# Revit family: Supply_Kit-Faucet-Waterworks-Universal-Angle-Compression
name_source: partatom
category: Plumbing Fixtures
revit_build: Autodesk Revit MEP 2014 (Build: 20140709_2115(x64)
units: mm (PartAtom-declared; Revit-internal decimal feet)

## types (16) — shared parameters
ADA Compliant = Yes
Assembly Code = D2010
CW Connection = Yes
Certification IAPMO = Yes
Certification NSF = Yes
Certification State of MA = Yes
Certification cUPC = Yes
Code Compliance = Code # FDMS32: Certified with IAPMO, NSF, City of LA & IAPMO-CA.
Cold Water Inlet Connection = Inlet - Compression
Cold Water Outlet Connection = Outlet- Compression
Default Elevation = 2' - 10"
Depth = 0' - 3 13/16"
HW Connection = Yes
Hot Limit Safety Stop = No
Hot Water Inlet Connection = Inlet - Compression
Hot Water Outlet Connection = Outlet - Compression
Inlet Connection Diameter = 0' - 0 1/2"
Keynote = 22 40 00
Length = 0' - 11"
Manufacturer = Waterworks
Model = UNMS32
Outlet Connection Diameter = 0' - 0 3/8"
Pressure = 45.00 psi
Product Documentation Link = http://assets.waterworks.com
Product Name = Universal Angle Faucet Supply Kits 1/2” Compression x 3/8” O.D. Compression
Product Page URL = http://www.waterworks.com
URL = http://www.waterworks.com
Vent Connection = No
Version = 2014 - v1.0a
Warranty = http://www.waterworks.com
Waste Connection = No
Water Pressure = Max: 85psi / Min: 20psi / Recommended: 45psi
‌Installation Requirements or Notes = Available option that complies with 0.25% Weighted Average Lead Content (WALC)
zero-valued in all types: CWFU, HWFU, WFU

## per-type parameters (varying)
| type | Constraint | Description | Finish | Model SKU |
| Antique Brass Complies with 0.25% WALC | 1 | Universal Angle Faucet Supply Kits 1/2” Compression x 3/8” O.D. Compression in Antique Brass Complies with 0.25% WALC | Metal - Waterworks - Antique Brass | 26-09876-57740 |
| Antique Copper Complies with 0.25% WALC | 2 | Universal Angle Faucet Supply Kits 1/2” Compression x 3/8” O.D. Compression in Antique Copper Complies with 0.25% WALC | Metal - Waterworks - Antique Copper | 26-73946-90196 |
| Architectural Bronze | 3 | Universal Angle Faucet Supply Kits 1/2” Compression x 3/8” O.D. Compression in Architectural Bronze | Metal - Waterworks - Architectural Bronze | 26-74676-98700 |
| Architectural Bronze Complies with 0.25% WALC | 4 | Universal Angle Faucet Supply Kits 1/2” Compression x 3/8” O.D. Compression in Architectural Bronze Complies with 0.25% WALC | Metal - Waterworks - Architectural Bronze | 26-70415-45280 |
| Burnished Brass Complies with 0.25% WALC | 6 | Universal Angle Faucet Supply Kits 1/2” Compression x 3/8” O.D. Compression in Burnished Brass Complies with 0.25% WALC | Metal - Waterworks - Burnished Brass | 26-48004-36693 |
| Burnished Nickel Complies with 0.25% WALC | 7 | Universal Angle Faucet Supply Kits 1/2” Compression x 3/8” O.D. Compression in Burnished Nickel Complies with 0.25% WALC | Metal - Waterworks - Burnished Nickel | 26-58991-27656 |
| Carbon Complies with 0.25% WALC | 8 | Universal Angle Faucet Supply Kits 1/2” Compression x 3/8” O.D. Compression in Carbon Complies with 0.25% WALC | Metal - Waterworks - Carbon | 26-06550-99717 |
| Chrome Complies with 0.25% WALC | 9 | Universal Angle Faucet Supply Kits 1/2” Compression x 3/8” O.D. Compression in Chrome Complies with 0.25% WALC | Metal - Waterworks - Chrome | 26-24536-85990 |
| Gold Complies with 0.25% WALC | 10 | Universal Angle Faucet Supply Kits 1/2” Compression x 3/8” O.D. Compression in Gold Complies with 0.25% WALC | Metal - Waterworks - Gold | 26-64518-46027 |
| Graphite | 11 | Universal Angle Faucet Supply Kits 1/2” Compression x 3/8” O.D. Compression in Graphite | Metal - Waterworks - Graphite | 26-14061-97142 |
| Matte Gold Complies with 0.25% WALC | 12 | Universal Angle Faucet Supply Kits 1/2” Compression x 3/8” O.D. Compression in Matte Gold Complies with 0.25% WALC | Metal - Waterworks - Matte Gold | 26-98562-70605 |
| Matte Nickel Complies with 0.25% WALC | 13 | Universal Angle Faucet Supply Kits 1/2” Compression x 3/8” O.D. Compression in Matte Nickel Complies with 0.25% WALC | Metal - Waterworks - Matte Nickel | 26-03683-66015 |
| Nickel Complies with 0.25% WALC | 14 | Universal Angle Faucet Supply Kits 1/2” Compression x 3/8” O.D. Compression in Nickel Complies with 0.25% WALC | Metal - Waterworks - Nickel | 26-23826-86137 |
| Pewter Complies with 0.25% WALC | 15 | Universal Angle Faucet Supply Kits 1/2” Compression x 3/8” O.D. Compression in Pewter Complies with 0.25% WALC | Metal - Waterworks - Pewter | 26-77848-04901 |
| Shiny Copper Complies with 0.25% WALC | 16 | Universal Angle Faucet Supply Kits 1/2” Compression x 3/8” O.D. Compression in Shiny Copper Complies with 0.25% WALC | Metal - Waterworks - Shiny Copper | 26-88317-94954 |
| Sovereign Complies with 0.25% WALC | 17 | Universal Angle Faucet Supply Kits 1/2” Compression x 3/8” O.D. Compression in Sovereign Complies with 0.25% WALC | Metal - Waterworks - Sovereign | 26-15093-03789 |

## geometry (parser evidence)
native form markers: Sweep x1
no freeform markers — native parametric forms only
